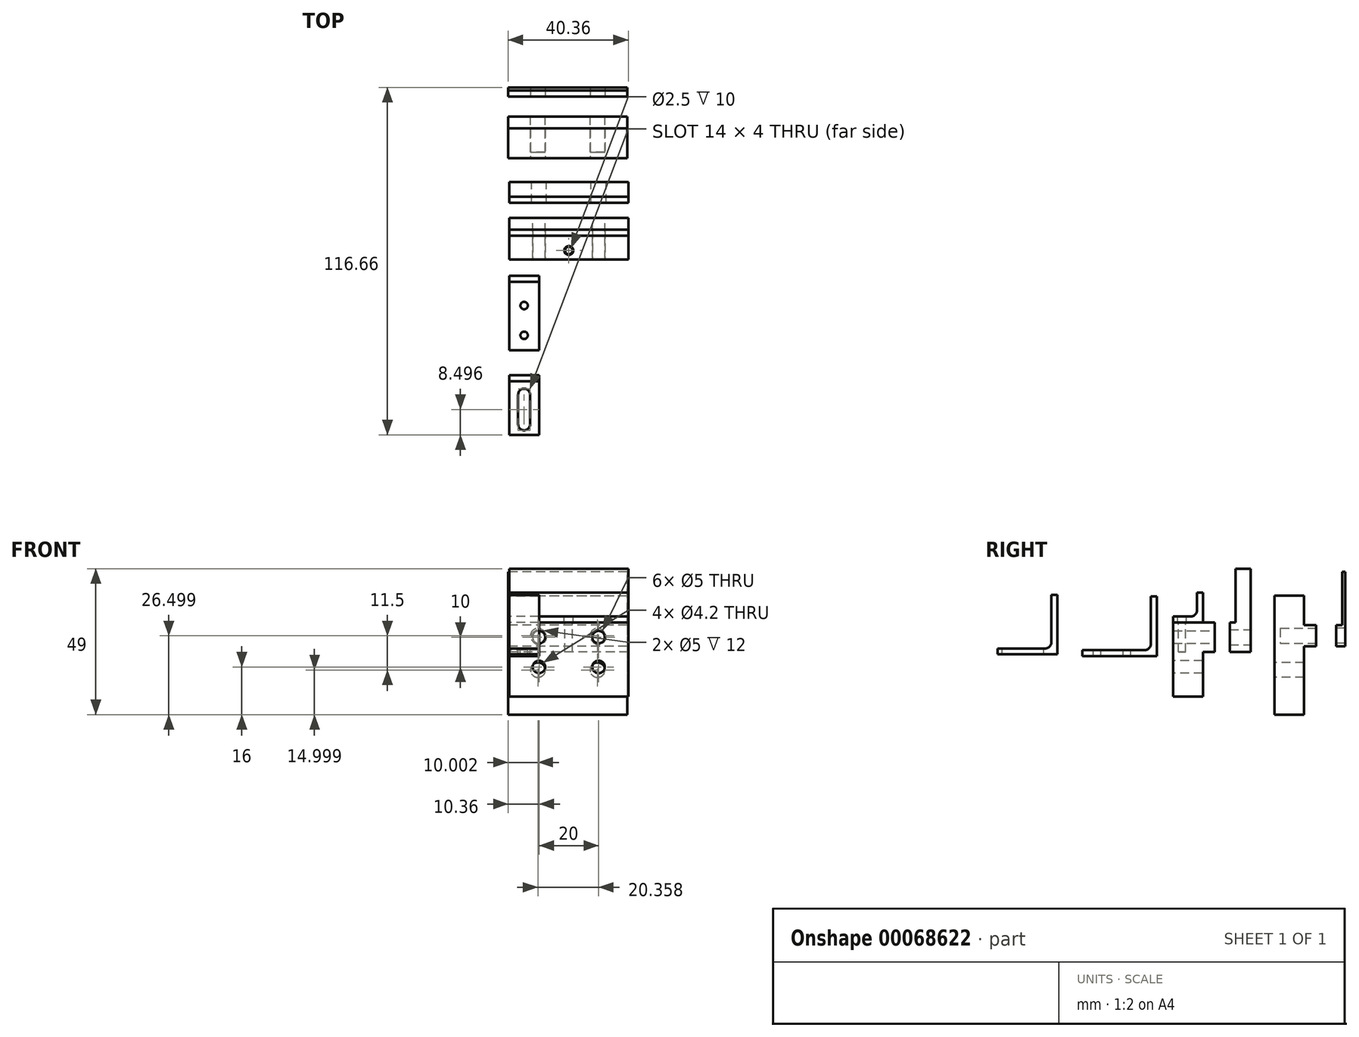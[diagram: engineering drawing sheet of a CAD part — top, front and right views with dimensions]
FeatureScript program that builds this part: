
annotation { "Feature Type Name" : "Feature", "Feature Type Description" : "" }
export const myFeature = defineFeature(function(context is Context, id is Id, definition is map)
    precondition{}
    {
        {
            var Q0;
            Q0=qCreatedBy(makeId("Right.planeOp"),FACE);
            cPlane(context, id + "F0", {"entities" : qUnion([Q0]), "cplaneType" : CPlaneType.OFFSET, "offset" : 40 * mm, "oppositeDirection" : true, "width" : 150 * mm, "height" : 150 * mm});
        }
        {
            var Q0;
            Q0=qCreatedBy(makeId("Front.planeOp"),FACE);
            var sketch = newSketch(context, id + "F1", { "sketchPlane" : qUnion([Q0])});
            skLineSegment(sketch, "E0.bottom", {"start": v(-40.36, 24) * mm, "end": v(-0.36, 24) * mm});
            skLineSegment(sketch, "E0.top", {"start": v(-40.36, -16) * mm, "end": v(-0.36, -16) * mm});
            skLineSegment(sketch, "E0.left", {"start": v(-40.36, 24) * mm, "end": v(-40.36, -16) * mm});
            skLineSegment(sketch, "E0.right", {"start": v(-0.36, 24) * mm, "end": v(-0.36, -16) * mm});
            skCircle(sketch, "E1", {"center": v(-10.36, -1) * mm, "radius": 2.5 * mm});
            skCircle(sketch, "E2", {"center": v(-30.36, -1) * mm, "radius": 2.5 * mm});
            skCircle(sketch, "E3", {"center": v(-30.36, -1) * mm, "radius": 6 * mm, "construction": true});
            skCircle(sketch, "E4", {"center": v(-10.36, -1) * mm, "radius": 6 * mm, "construction": true});
            skSolve(sketch);
        }
        {
            var Q0;
            Q0 = qSketchRegion(id + "F1", true);
            extrude(context, id + "F2", {"entities" : qUnion([Q0]), "oppositeDirection" : true, "depth" : 10 * mm});
        }
        {
            var Q0;
            Q0=makeQuery(id+"F2.opExtrude","CAP_FACE",FACE,{"disambiguationData":[OSD([sQuery(id+"F1.wireOp",EDGE,"E0.bottom"),sQuery(id+"F1.wireOp",EDGE,"E0.top"),sQuery(id+"F1.wireOp",EDGE,"E0.left"),sQuery(id+"F1.wireOp",EDGE,"E0.right"),sQuery(id+"F1.wireOp",EDGE,"E1"),sQuery(id+"F1.wireOp",EDGE,"E2")])],"isStart":false});
            var sketch = newSketch(context, id + "F3", { "sketchPlane" : qUnion([Q0])});
            skLineSegment(sketch, "E5.bottom", {"start": v(0.36, 14) * mm, "end": v(40.36, 14) * mm});
            skLineSegment(sketch, "E5.top", {"start": v(0.36, 7) * mm, "end": v(40.36, 7) * mm});
            skLineSegment(sketch, "E5.left", {"start": v(0.36, 14) * mm, "end": v(0.36, 7) * mm});
            skLineSegment(sketch, "E5.right", {"start": v(40.36, 14) * mm, "end": v(40.36, 7) * mm});
            skSolve(sketch);
        }
        {
            var Q0;
            Q0 = qSketchRegion(id + "F3", true);
            extrude(context, id + "F4", {"entities" : qUnion([Q0]), "operationType" : NewBodyOperationType.ADD, "depth" : 4 * mm});
        }
        {
            var Q0;
            Q0=makeQuery(id+"F4.opExtrude","CAP_FACE",FACE,{"disambiguationData":[OSD([sQuery(id+"F3.wireOp",EDGE,"E5.bottom"),sQuery(id+"F3.wireOp",EDGE,"E5.top"),sQuery(id+"F3.wireOp",EDGE,"E5.left"),sQuery(id+"F3.wireOp",EDGE,"E5.right")])],"isStart":false});
            var sketch = newSketch(context, id + "F5", { "sketchPlane" : qUnion([Q0])});
            skCircle(sketch, "E6", {"center": v(10.36, 10.5) * mm, "radius": 2.5 * mm});
            skCircle(sketch, "E7", {"center": v(30.36, 10.5) * mm, "radius": 2.5 * mm});
            skSolve(sketch);
        }
        {
            var Q0;
            Q0 = qSketchRegion(id + "F5", true);
            extrude(context, id + "F6", {"entities" : qUnion([Q0]), "operationType" : NewBodyOperationType.REMOVE, "oppositeDirection" : true, "depth" : 12 * mm});
        }
        {
            var Q0;
            Q0=makeQuery(id+"F4.boolean.opBoolean","MERGE",FACE,{"derivedFrom":[makeQuery(id+"F2.opExtrude","SWEPT_FACE",FACE,{"disambiguationData":[OSD([sQuery(id+"F1.wireOp",EDGE,"E0.left")])]}),makeQuery(id+"F4.opExtrude","SWEPT_FACE",FACE,{"disambiguationData":[OSD([sQuery(id+"F3.wireOp",EDGE,"E5.right")])]})]});
            var sketch = newSketch(context, id + "F7", { "sketchPlane" : qUnion([Q0])});
            skLineSegment(sketch, "E8", {"start": v(-23.76, 32) * mm, "end": v(-23.76, 7) * mm});
            skLineSegment(sketch, "E9", {"start": v(-20.76, 7) * mm, "end": v(-23.76, 7) * mm});
            skLineSegment(sketch, "E10", {"start": v(-20.76, 7) * mm, "end": v(-20.76, 14) * mm});
            skLineSegment(sketch, "E11", {"start": v(-22.76, 14) * mm, "end": v(-20.76, 14) * mm});
            skLineSegment(sketch, "E12", {"start": v(-22.76, 14) * mm, "end": v(-22.76, 32) * mm});
            skLineSegment(sketch, "E13", {"start": v(-23.76, 32) * mm, "end": v(-22.76, 32) * mm});
            skSolve(sketch);
        }
        {
            var Q0;
            Q0=makeQuery(id+"F7.imprint","IMPRINT",FACE,{"disambiguationData":[TD([[makeQuery(id+"F7.imprint","IMPRINT",EDGE,{"derivedFrom":sQuery(id+"F7.wireOp",EDGE,"E8")}),1.0]])]});
            extrude(context, id + "F8", {"entities" : qUnion([Q0]), "oppositeDirection" : true, "depth" : 40 * mm});
        }
        {
            var Q0;
            Q0=makeQuery(id+"F8.opExtrude","SWEPT_FACE",FACE,{"disambiguationData":[OSD([sQuery(id+"F7.wireOp",EDGE,"E10")])]});
            var sketch = newSketch(context, id + "F9", { "sketchPlane" : qUnion([Q0])});
            skCircle(sketch, "E14", {"center": v(-30.36, 10.5) * mm, "radius": 2.5 * mm});
            skCircle(sketch, "E15", {"center": v(-10.36, 10.5) * mm, "radius": 2.5 * mm});
            skSolve(sketch);
        }
        {
            var Q0;
            Q0=makeQuery(id+"F9.imprint","IMPRINT",FACE,{"disambiguationData":[TD([[makeQuery(id+"F9.imprint","IMPRINT",EDGE,{"derivedFrom":sQuery(id+"F9.wireOp",EDGE,"E14")}),1.0]])]});
            var Q1;
            Q1=makeQuery(id+"F9.imprint","IMPRINT",FACE,{"disambiguationData":[TD([[makeQuery(id+"F9.imprint","IMPRINT",EDGE,{"derivedFrom":sQuery(id+"F9.wireOp",EDGE,"E15")}),1.0]])]});
            extrude(context, id + "F10", {"entities" : qUnion([Q0, Q1]), "operationType" : NewBodyOperationType.REMOVE, "oppositeDirection" : true, "depth" : 3 * mm});
        }
        {
            var Q0;
            Q0=qCreatedBy(id+"F0.planeOp",FACE);
            var sketch = newSketch(context, id + "F11", { "sketchPlane" : qUnion([Q0])});
            skLineSegment(sketch, "E16", {"start": v(-20, 15) * mm, "end": v(-34, 15) * mm});
            skLineSegment(sketch, "E17", {"start": v(-34, 15) * mm, "end": v(-34, -10) * mm});
            skLineSegment(sketch, "E18", {"start": v(-34, -10) * mm, "end": v(-24, -10) * mm});
            skLineSegment(sketch, "E19", {"start": v(-24, -10) * mm, "end": v(-24, 5) * mm});
            skLineSegment(sketch, "E20", {"start": v(-24, 5) * mm, "end": v(-20, 5) * mm});
            skLineSegment(sketch, "E21", {"start": v(-20, 5) * mm, "end": v(-20, 15) * mm});
            skSolve(sketch);
        }
        {
            var Q0;
            Q0 = qSketchRegion(id + "F11", true);
            extrude(context, id + "F12", {"entities" : qUnion([Q0]), "depth" : 40 * mm});
        }
        {
            var Q0;
            Q0=qCreatedBy(id+"F0.planeOp",FACE);
            var sketch = newSketch(context, id + "F13", { "sketchPlane" : qUnion([Q0])});
            skLineSegment(sketch, "E22", {"start": v(-8, 33) * mm, "end": v(-8, 5) * mm});
            skLineSegment(sketch, "E23", {"start": v(-8, 5) * mm, "end": v(-15, 5) * mm});
            skLineSegment(sketch, "E24", {"start": v(-15, 5) * mm, "end": v(-15, 15) * mm});
            skLineSegment(sketch, "E25", {"start": v(-15, 15) * mm, "end": v(-13, 15) * mm});
            skLineSegment(sketch, "E26", {"start": v(-13, 15) * mm, "end": v(-13, 33) * mm});
            skLineSegment(sketch, "E27", {"start": v(-13, 33) * mm, "end": v(-8, 33) * mm});
            skSolve(sketch);
        }
        {
            var Q0;
            Q0=makeQuery(id+"F13.imprint","IMPRINT",FACE,{"disambiguationData":[TD([[makeQuery(id+"F13.imprint","IMPRINT",EDGE,{"derivedFrom":sQuery(id+"F13.wireOp",EDGE,"E22")}),-1.0]])]});
            extrude(context, id + "F14", {"entities" : qUnion([Q0]), "depth" : 40 * mm});
        }
        {
            var Q0;
            Q0=makeQuery(id+"F12.opExtrude","SWEPT_FACE",FACE,{"disambiguationData":[OSD([sQuery(id+"F11.wireOp",EDGE,"E17")])]});
            var sketch = newSketch(context, id + "F15", { "sketchPlane" : qUnion([Q0])});
            skCircle(sketch, "E28", {"center": v(-30, 0) * mm, "radius": 2.1 * mm});
            skCircle(sketch, "E29", {"center": v(-10, 0) * mm, "radius": 2.1 * mm});
            skSolve(sketch);
        }
        {
            var Q0;
            Q0=makeQuery(id+"F14.opExtrude","SWEPT_FACE",FACE,{"disambiguationData":[OSD([sQuery(id+"F13.wireOp",EDGE,"E22")])]});
            var sketch = newSketch(context, id + "F16", { "sketchPlane" : qUnion([Q0])});
            skCircle(sketch, "E30", {"center": v(10, 10) * mm, "radius": 2.5 * mm});
            skCircle(sketch, "E31", {"center": v(30, 10) * mm, "radius": 2.5 * mm});
            skSolve(sketch);
        }
        {
            var Q0;
            Q0=qCreatedBy(id+"F0.planeOp",FACE);
            var sketch = newSketch(context, id + "F17", { "sketchPlane" : qUnion([Q0])});
            skLineSegment(sketch, "E32", {"start": v(-24, 25) * mm, "end": v(-24, 15) * mm});
            skLineSegment(sketch, "E33", {"start": v(-24, 15) * mm, "end": v(-34, 15) * mm});
            skLineSegment(sketch, "E34", {"start": v(-34, 15) * mm, "end": v(-34, 17) * mm});
            skLineSegment(sketch, "E35", {"start": v(-34, 17) * mm, "end": v(-28, 17) * mm});
            skLineSegment(sketch, "E36", {"start": v(-26, 19) * mm, "end": v(-26, 25) * mm});
            skLineSegment(sketch, "E37", {"start": v(-26, 25) * mm, "end": v(-24, 25) * mm});
            skPoint(sketch, "E38.visualSharp", {"position": v(-26, 17) * mm});
            skArc(sketch, "E38.filletArc", {"start": v(-28, 17) * mm, "mid": v(-26.59, 17.59) * mm, "end": v(-26, 19) * mm});
            skSolve(sketch);
        }
        {
            var Q0;
            Q0=makeQuery(id+"F17.imprint","IMPRINT",FACE,{"disambiguationData":[TD([[makeQuery(id+"F17.imprint","IMPRINT",EDGE,{"derivedFrom":sQuery(id+"F17.wireOp",EDGE,"E32")}),-1.0]])]});
            extrude(context, id + "F18", {"entities" : qUnion([Q0]), "depth" : 40 * mm});
        }
        {
            var Q0;
            Q0=makeQuery(id+"F18.opExtrude","SWEPT_FACE",FACE,{"disambiguationData":[OSD([sQuery(id+"F17.wireOp",EDGE,"E35")])]});
            var sketch = newSketch(context, id + "F19", { "sketchPlane" : qUnion([Q0])});
            skCircle(sketch, "E39", {"center": v(-20, -31) * mm, "radius": 1.25 * mm});
            skSolve(sketch);
        }
        {
            var Q0;
            Q0=makeQuery(id+"F15.imprint","IMPRINT",FACE,{"disambiguationData":[TD([[makeQuery(id+"F15.imprint","IMPRINT",EDGE,{"derivedFrom":sQuery(id+"F15.wireOp",EDGE,"E28")}),1.0]])]});
            var Q1;
            Q1=makeQuery(id+"F15.imprint","IMPRINT",FACE,{"disambiguationData":[TD([[makeQuery(id+"F15.imprint","IMPRINT",EDGE,{"derivedFrom":sQuery(id+"F15.wireOp",EDGE,"E29")}),1.0]])]});
            extrude(context, id + "F20", {"entities" : qUnion([Q0, Q1]), "operationType" : NewBodyOperationType.REMOVE, "oppositeDirection" : true, "depth" : 10 * mm});
        }
        {
            var Q0;
            Q0=makeQuery(id+"F16.imprint","IMPRINT",FACE,{"disambiguationData":[TD([[makeQuery(id+"F16.imprint","IMPRINT",EDGE,{"derivedFrom":sQuery(id+"F16.wireOp",EDGE,"E30")}),1.0]])]});
            var Q1;
            Q1=makeQuery(id+"F16.imprint","IMPRINT",FACE,{"disambiguationData":[TD([[makeQuery(id+"F16.imprint","IMPRINT",EDGE,{"derivedFrom":sQuery(id+"F16.wireOp",EDGE,"E31")}),1.0]])]});
            extrude(context, id + "F21", {"entities" : qUnion([Q0, Q1]), "operationType" : NewBodyOperationType.REMOVE, "oppositeDirection" : true, "depth" : 7 * mm});
        }
        {
            var Q0;
            Q0=makeQuery(id+"F19.imprint","IMPRINT",FACE,{"disambiguationData":[TD([[makeQuery(id+"F19.imprint","IMPRINT",EDGE,{"derivedFrom":sQuery(id+"F19.wireOp",EDGE,"nTF4TsUg-xscX-gh34-UHNV-MDi5rEr1EhpZ")}),1.0]])]});
            var Q1;
            Q1=makeQuery(id+"F19.imprint","IMPRINT",FACE,{"disambiguationData":[TD([[makeQuery(id+"F19.imprint","IMPRINT",EDGE,{"derivedFrom":sQuery(id+"F19.wireOp",EDGE,"E39")}),1.0]])]});
            extrude(context, id + "F22", {"entities" : qUnion([Q0, Q1]), "operationType" : NewBodyOperationType.REMOVE, "oppositeDirection" : true, "depth" : 12 * mm});
        }
        {
            var Q0;
            Q0=qCreatedBy(id+"F0.planeOp",FACE);
            var sketch = newSketch(context, id + "F23", { "sketchPlane" : qUnion([Q0])});
            skLineSegment(sketch, "E40", {"start": v(-39.5, 23.68) * mm, "end": v(-39.5, 3.68) * mm});
            skLineSegment(sketch, "E41", {"start": v(-39.5, 3.68) * mm, "end": v(-64.5, 3.68) * mm});
            skLineSegment(sketch, "E42", {"start": v(-64.5, 3.68) * mm, "end": v(-64.5, 5.68) * mm});
            skLineSegment(sketch, "E43", {"start": v(-64.5, 5.68) * mm, "end": v(-43.5, 5.68) * mm});
            skLineSegment(sketch, "E44", {"start": v(-41.5, 7.68) * mm, "end": v(-41.5, 23.68) * mm});
            skLineSegment(sketch, "E45", {"start": v(-41.5, 23.68) * mm, "end": v(-39.5, 23.68) * mm});
            skPoint(sketch, "E46.visualSharp", {"position": v(-41.5, 5.68) * mm});
            skArc(sketch, "E46.filletArc", {"start": v(-43.5, 5.68) * mm, "mid": v(-42.08, 6.26) * mm, "end": v(-41.5, 7.68) * mm});
            skSolve(sketch);
        }
        {
            var Q0;
            Q0=makeQuery(id+"F23.imprint","IMPRINT",FACE,{"disambiguationData":[TD([[makeQuery(id+"F23.imprint","IMPRINT",EDGE,{"derivedFrom":sQuery(id+"F23.wireOp",EDGE,"E40")}),-1.0]])]});
            extrude(context, id + "F24", {"entities" : qUnion([Q0]), "depth" : 10 * mm});
        }
        {
            var Q0;
            Q0=makeQuery(id+"F24.opExtrude","SWEPT_FACE",FACE,{"disambiguationData":[OSD([sQuery(id+"F23.wireOp",EDGE,"E43")])]});
            var sketch = newSketch(context, id + "F25", { "sketchPlane" : qUnion([Q0])});
            skCircle(sketch, "E47", {"center": v(-35, -49.5) * mm, "radius": 1.25 * mm});
            skCircle(sketch, "E48", {"center": v(-35, -59.5) * mm, "radius": 1.25 * mm});
            skSolve(sketch);
        }
        {
            var Q0;
            Q0=makeQuery(id+"F25.imprint","IMPRINT",FACE,{"disambiguationData":[TD([[makeQuery(id+"F25.imprint","IMPRINT",EDGE,{"derivedFrom":sQuery(id+"F25.wireOp",EDGE,"E47")}),1.0]])]});
            var Q1;
            Q1=makeQuery(id+"F25.imprint","IMPRINT",FACE,{"disambiguationData":[TD([[makeQuery(id+"F25.imprint","IMPRINT",EDGE,{"derivedFrom":sQuery(id+"F25.wireOp",EDGE,"E48")}),1.0]])]});
            extrude(context, id + "F26", {"entities" : qUnion([Q0, Q1]), "operationType" : NewBodyOperationType.REMOVE, "oppositeDirection" : true, "depth" : 2 * mm});
        }
        {
            var Q0;
            Q0=qCreatedBy(id+"F0.planeOp",FACE);
            var sketch = newSketch(context, id + "F27", { "sketchPlane" : qUnion([Q0])});
            skLineSegment(sketch, "E49", {"start": v(-72.9, 24.22) * mm, "end": v(-72.9, 4.22) * mm});
            skLineSegment(sketch, "E50", {"start": v(-72.9, 4.22) * mm, "end": v(-92.9, 4.22) * mm});
            skLineSegment(sketch, "E51", {"start": v(-92.9, 4.22) * mm, "end": v(-92.9, 6.22) * mm});
            skLineSegment(sketch, "E52", {"start": v(-92.9, 6.22) * mm, "end": v(-76.9, 6.22) * mm});
            skLineSegment(sketch, "E53", {"start": v(-74.9, 8.22) * mm, "end": v(-74.9, 24.22) * mm});
            skLineSegment(sketch, "E54", {"start": v(-74.9, 24.22) * mm, "end": v(-72.9, 24.22) * mm});
            skPoint(sketch, "E55.visualSharp", {"position": v(-74.9, 6.22) * mm});
            skArc(sketch, "E55.filletArc", {"start": v(-76.9, 6.22) * mm, "mid": v(-75.5, 6.8) * mm, "end": v(-74.9, 8.22) * mm});
            skSolve(sketch);
        }
        {
            var Q0;
            Q0=makeQuery(id+"F27.imprint","IMPRINT",FACE,{"disambiguationData":[TD([[makeQuery(id+"F27.imprint","IMPRINT",EDGE,{"derivedFrom":sQuery(id+"F27.wireOp",EDGE,"E49")}),-1.0]])]});
            var Q1;
            Q1=sQuery(id+"F27.wireOp",EDGE,"E49");
            var Q2;
            Q2=sQuery(id+"F27.wireOp",EDGE,"E50");
            var Q3;
            Q3=sQuery(id+"F27.wireOp",EDGE,"E51");
            var Q4;
            Q4=sQuery(id+"F27.wireOp",EDGE,"E52");
            var Q5;
            Q5=sQuery(id+"F27.wireOp",EDGE,"E53");
            var Q6;
            Q6=sQuery(id+"F27.wireOp",EDGE,"E54");
            extrude(context, id + "F28", {"entities" : qUnion([Q0]), "surfaceEntities" : qUnion([Q1, Q2, Q3, Q4, Q5, Q6]), "depth" : 10 * mm});
        }
        {
            var Q0;
            Q0=makeQuery(id+"F28.opExtrude","SWEPT_FACE",FACE,{"disambiguationData":[OSD([sQuery(id+"F27.wireOp",EDGE,"E52")])]});
            var sketch = newSketch(context, id + "F29", { "sketchPlane" : qUnion([Q0])});
            skLineSegment(sketch, "E56.left", {"start": v(-37, -89.4) * mm, "end": v(-37, -79.4) * mm});
            skLineSegment(sketch, "E56.right", {"start": v(-33, -89.4) * mm, "end": v(-33, -79.4) * mm});
            skPoint(sketch, "E56.middle", {"position": v(-35, -84.4) * mm});
            skArc(sketch, "E57", {"start": v(-37, -89.4) * mm, "mid": v(-35, -91.4) * mm, "end": v(-33, -89.4) * mm});
            skArc(sketch, "E58", {"start": v(-33, -79.4) * mm, "mid": v(-35, -77.4) * mm, "end": v(-37, -79.4) * mm});
            skSolve(sketch);
        }
        {
            var Q0;
            Q0=makeQuery(id+"F29.imprint","IMPRINT",FACE,{"disambiguationData":[TD([[makeQuery(id+"F29.imprint","IMPRINT",EDGE,{"derivedFrom":sQuery(id+"F29.wireOp",EDGE,"E56.left")}),-1.0]])]});
            extrude(context, id + "F30", {"entities" : qUnion([Q0]), "operationType" : NewBodyOperationType.REMOVE, "oppositeDirection" : true, "depth" : 3 * mm});
        }
        {
            var Q0;
            Q0=makeQuery(id+"F12.opExtrude","SWEPT_FACE",FACE,{"disambiguationData":[OSD([sQuery(id+"F11.wireOp",EDGE,"E21")])]});
            var sketch = newSketch(context, id + "F31", { "sketchPlane" : qUnion([Q0])});
            skCircle(sketch, "E59", {"center": v(30, 10) * mm, "radius": 2.1 * mm});
            skCircle(sketch, "E60", {"center": v(10, 10) * mm, "radius": 2.1 * mm});
            skSolve(sketch);
        }
        {
            var Q0;
            Q0 = qSketchRegion(id + "F31", true);
            extrude(context, id + "F32", {"entities" : qUnion([Q0]), "operationType" : NewBodyOperationType.REMOVE, "oppositeDirection" : true, "depth" : 14 * mm});
        }
        {
            var Q0;
            Q0=sQuery(id+"F19.wireOp",VERTEX,"E39.center");
            var Q1;
            Q1=makeQuery(id+"F18.opExtrude","SWEPT_BODY",BODY,{"disambiguationData":[OSD([sQuery(id+"F17.wireOp",EDGE,"E32"),sQuery(id+"F17.wireOp",EDGE,"E33"),sQuery(id+"F17.wireOp",EDGE,"E34"),sQuery(id+"F17.wireOp",EDGE,"E35"),sQuery(id+"F17.wireOp",EDGE,"E36"),sQuery(id+"F17.wireOp",EDGE,"E37"),sQuery(id+"F17.wireOp",EDGE,"E38.filletArc")])]});
            hole(context, id + "F33", {"style" : HoleStyle.SIMPLE, "endStyle" : HoleEndStyle.THROUGH, "holeDiameter" : 3 * mm, "locations" : qUnion([Q0]), "scope" : qUnion([Q1]), "isTappedThrough" : true});
        }
    });
